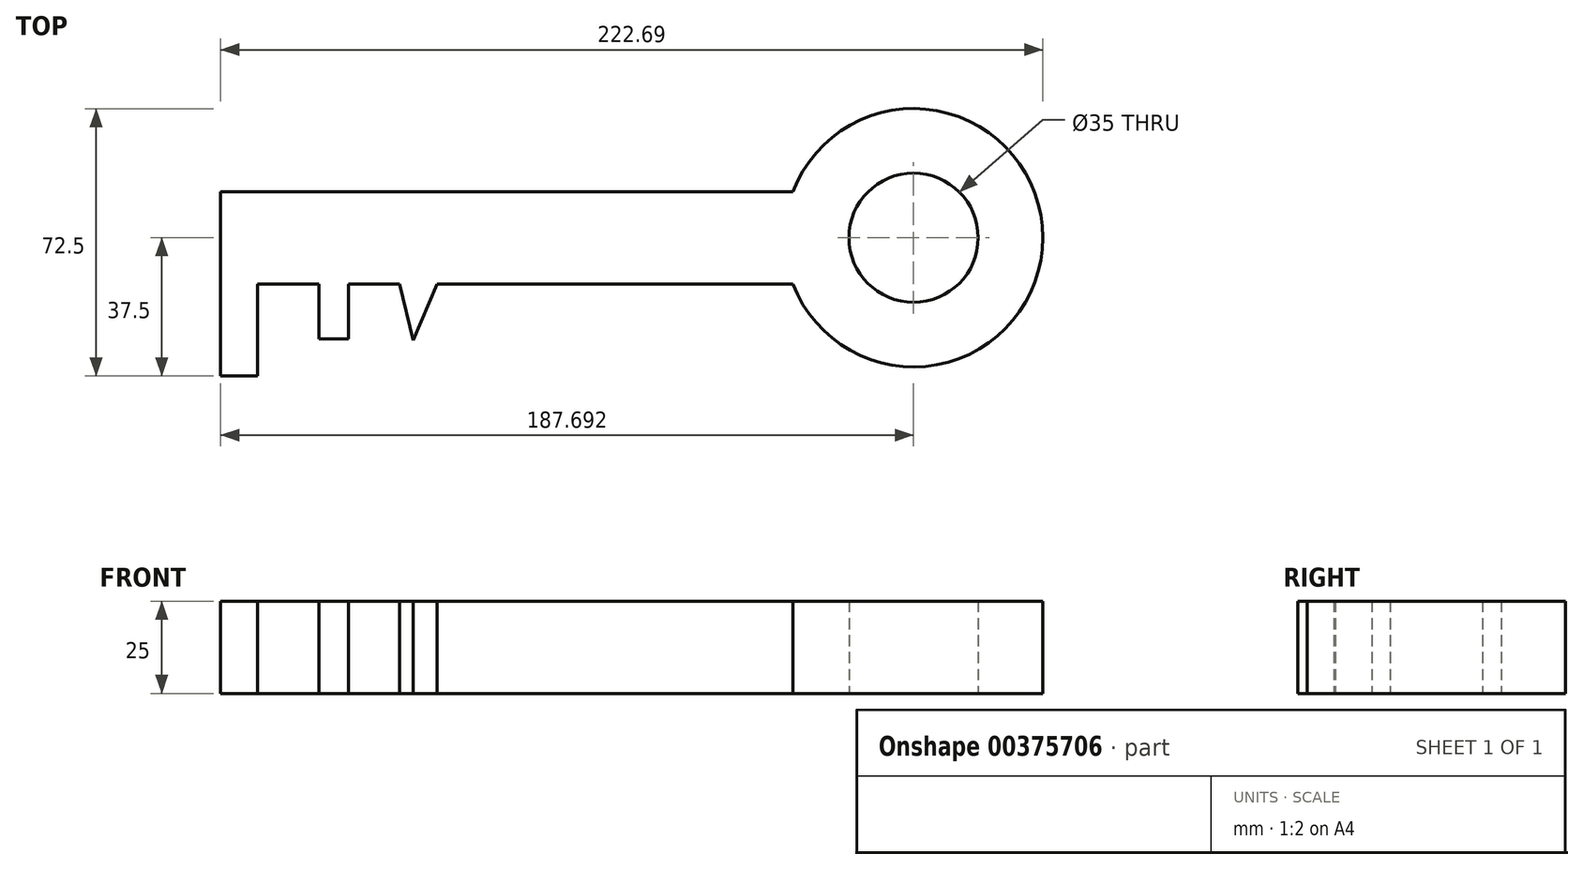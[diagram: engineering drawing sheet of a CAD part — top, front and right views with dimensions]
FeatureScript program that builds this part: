
annotation { "Feature Type Name" : "Feature", "Feature Type Description" : "" }
export const myFeature = defineFeature(function(context is Context, id is Id, definition is map)
    precondition{}
    {
        {
            var Q0;
            Q0=qCreatedBy(makeId("Top.planeOp"),FACE);
            var sketch = newSketch(context, id + "F0", { "sketchPlane" : qUnion([Q0])});
            skLineSegment(sketch, "E0.bottom", {"start": v(0, 0) * mm, "end": v(-155, 0) * mm});
            skLineSegment(sketch, "E0.top", {"start": v(0, 25) * mm, "end": v(-155, 25) * mm});
            skLineSegment(sketch, "E0.left", {"start": v(0, 0) * mm, "end": v(0, 25) * mm});
            skLineSegment(sketch, "E0.right", {"start": v(-155, 0) * mm, "end": v(-155, 25) * mm});
            skLineSegment(sketch, "E1.bottom", {"start": v(-155, 0) * mm, "end": v(-145, 0) * mm});
            skLineSegment(sketch, "E1.top", {"start": v(-155, -25) * mm, "end": v(-145, -25) * mm});
            skLineSegment(sketch, "E1.left", {"start": v(-155, 0) * mm, "end": v(-155, -25) * mm});
            skLineSegment(sketch, "E1.right", {"start": v(-145, 0) * mm, "end": v(-145, -25) * mm});
            skLineSegment(sketch, "E2.bottom", {"start": v(-128.4, 0) * mm, "end": v(-120.4, 0) * mm});
            skLineSegment(sketch, "E2.top", {"start": v(-128.4, -14.94) * mm, "end": v(-120.4, -14.94) * mm});
            skLineSegment(sketch, "E2.left", {"start": v(-128.4, 0) * mm, "end": v(-128.4, -14.94) * mm});
            skLineSegment(sketch, "E2.right", {"start": v(-120.4, 0) * mm, "end": v(-120.4, -14.94) * mm});
            skArc(sketch, "E3", {"start": v(0, 0) * mm, "mid": v(67.7, 12.5) * mm, "end": v(0, 25) * mm});
            skCircle(sketch, "E4", {"center": v(32.7, 12.5) * mm, "radius": 17.5 * mm});
            skLineSegment(sketch, "E5", {"start": v(-106.5, 0) * mm, "end": v(-102.87, -15.24) * mm});
            skLineSegment(sketch, "E6", {"start": v(-102.87, -15.24) * mm, "end": v(-96.45, 0) * mm});
            skLineSegment(sketch, "E7", {"start": v(32.7, 12.5) * mm, "end": v(-155, 12.5) * mm, "construction": true});
            skSolve(sketch);
        }
        {
            var Q0;
            Q0 = qSketchRegion(id + "F0", true);
            extrude(context, id + "F1", {"entities" : qUnion([Q0]), "depth" : 25 * mm});
        }
    });
